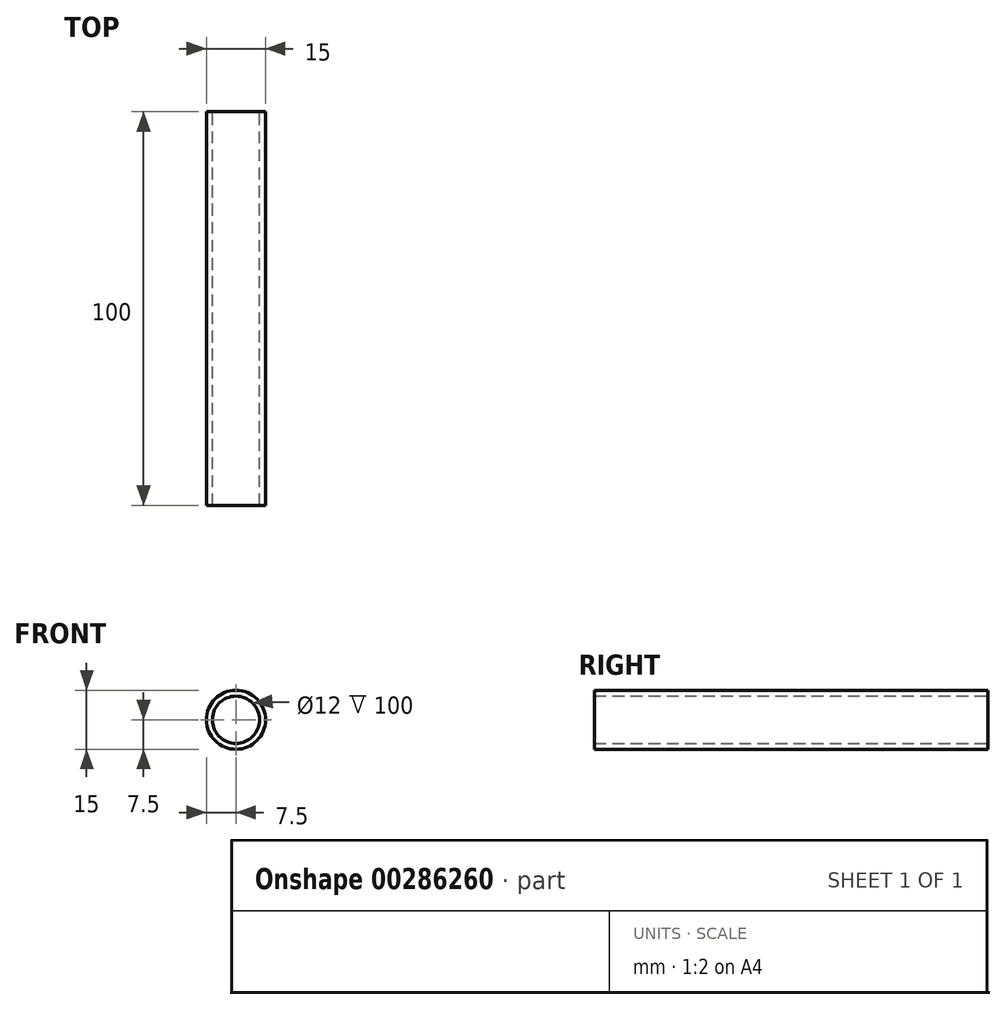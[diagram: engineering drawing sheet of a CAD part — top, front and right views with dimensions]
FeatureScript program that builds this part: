
annotation { "Feature Type Name" : "Feature", "Feature Type Description" : "" }
export const myFeature = defineFeature(function(context is Context, id is Id, definition is map)
    precondition{}
    {
        {
            var Q0;
            Q0=qCreatedBy(makeId("Front.planeOp"),FACE);
            var sketch = newSketch(context, id + "F0", { "sketchPlane" : qUnion([Q0])});
            skCircle(sketch, "E0", {"center": v(0, 0) * mm, "radius": 7.5 * mm});
            skCircle(sketch, "E1", {"center": v(0, 0) * mm, "radius": 6 * mm});
            skSolve(sketch);
        }
        {
            var Q0;
            Q0=qSketchRegion(id+"F0",true);
            extrude(context, id + "F1", {"entities" : qUnion([Q0]), "depth" : 100 * mm});
        }
    });
